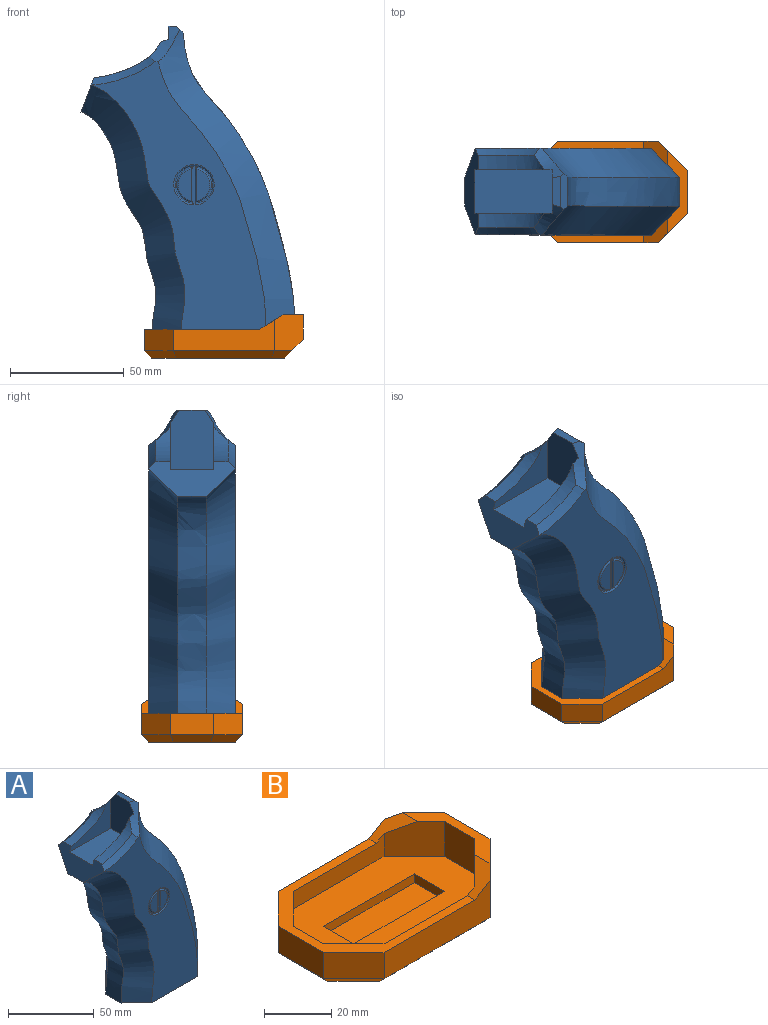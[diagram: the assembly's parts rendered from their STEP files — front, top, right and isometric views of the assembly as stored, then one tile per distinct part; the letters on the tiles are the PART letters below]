
ASSEMBLY  parts=2 mates=1
PART A: 44 faces, bbox 96.5x41.4x146.9 mm
  f0: plane 38.11x15.14mm, normal (-0.93,0,0.36), area 372.2mm2, adj f2,f3,f4,f9,f10,f13,f14,f15
  f1: plane 13.53x3.63mm, normal (0,0,1), area 45mm2, adj f16,f19,f20,f21
  f2: extruded ~29.2x15.61mm, area 194.8mm2, adj f0,f14,f18,f20
  f3: extruded ~29.2x15.61mm, area 194.9mm2, adj f0,f15,f17,f19
  f4: extruded ~101.84x33.05mm, area 1417.9mm2, adj f0,f5,f9,f10
  f5: plane 60.95x38.1mm, normal (0,0,-1), area 1573.9mm2, adj f4,f7,f8,f9,f10,f11,f12,f22
  f6: extruded ~133.98x49.47mm, area 1855.8mm2, adj f11,f12,f21,f43
  f7: plane 126.11x79.17mm, normal (0,-1,0), area 3830.8mm2, adj f5,f10,f12,f17,f19,f34
  f8: plane 126.11x79.17mm, normal (0,1,0), area 3832.2mm2, adj f5,f9,f11,f18,f20,f40
  f9: bspline ~118.13x45.8mm, area 2100.8mm2, adj f0,f4,f5,f8,f18
  f10: bspline ~118.13x45.8mm, area 2136.8mm2, adj f0,f4,f5,f7,f17
  f11: bspline ~138.88x62.18mm, area 2560.7mm2, adj f5,f6,f8,f20,f21,f43
  f12: bspline ~138.88x62.18mm, area 2560.7mm2, adj f5,f6,f7,f19,f21,f43
  f13: plane 33.95x19.05mm, normal (0,0,1), area 646.8mm2, adj f0,f14,f15,f16
  f14: plane 34.17x20.64mm, normal (0,-1,0), area 311.9mm2, adj f0,f2,f13,f16,f20
  f15: plane 34.17x20.64mm, normal (0,1,0), area 311.9mm2, adj f0,f3,f13,f16,f19
  f16: plane 26.8x19.58mm, normal (-1,0,0), area 478.3mm2, adj f1,f13,f14,f15,f19,f20
  f17: bspline ~30.63x14.14mm, area 128.4mm2, adj f0,f3,f7,f10,f19
  f18: bspline ~30.63x14.14mm, area 128.3mm2, adj f0,f2,f8,f9,f20
  f19: bspline ~17.85x15.06mm, area 103mm2, adj f1,f3,f7,f12,f15,f16,f17,f21
  f20: bspline ~17.86x15.07mm, area 103mm2, adj f1,f2,f8,f11,f14,f16,f18,f21
  f21: plane 16.15x3.24mm, normal (0.7,0,0.71), area 65.1mm2, adj f1,f6,f11,f12,f19,f20
  f22: plane 38.09x3.18mm, normal (0,-1,0), area 120.9mm2, adj f5,f23,f25,f26
  f23: plane 12.7x3.18mm, normal (-1,0,0), area 40.3mm2, adj f5,f22,f24,f26
  f24: plane 38.09x3.18mm, normal (0,1,0), area 120.9mm2, adj f5,f23,f25,f26
  f25: plane 12.7x3.18mm, normal (1,0,0), area 40.3mm2, adj f5,f22,f24,f26
  f26: plane 38.09x12.7mm, normal (0,0,-1), area 483.8mm2, adj f22,f23,f24,f25
  f27: plane 16.51x16.51mm, normal (0,-1,0), area 47.1mm2, adj f30,f31,f32,f33,f34
  f28: plane 13.78x5.84mm, normal (0,-1,0), area 60.7mm2, adj f32,f33
  f29: plane 13.78x5.84mm, normal (0,-1,0), area 60.7mm2, adj f30,f31
  f30: torus R=6.99mm, axis (0,-1,0), area 21.5mm2, adj f27,f29,f31
  f31: cylinder r=0.64mm len=15.21mm, axis (0,0,-1), area 14.5mm2, adj f27,f29,f30
  f32: cylinder r=0.64mm len=15.21mm, axis (0,0,1), area 14.5mm2, adj f27,f28,f33
  f33: torus R=6.99mm, axis (0,-1,0), area 21.5mm2, adj f27,f28,f32
  f34: torus R=8.89mm, axis (0,-1,0), area 53.2mm2, adj f7,f27
  f35: plane 16.51x16.51mm, normal (0,1,0), area 47.1mm2, adj f38,f39,f40,f41,f42
  f36: plane 13.78x5.84mm, normal (0,1,0), area 60.7mm2, adj f41,f42
  f37: plane 13.78x5.84mm, normal (0,1,0), area 60.7mm2, adj f38,f39
  f38: torus R=6.99mm, axis (0,-1,0), area 21.5mm2, adj f35,f37,f39
  f39: cylinder r=0.64mm len=15.21mm, axis (0,0,1), area 14.5mm2, adj f35,f37,f38
  f40: torus R=8.89mm, axis (0,-1,0), area 53.2mm2, adj f8,f35
  f41: cylinder r=0.64mm len=15.21mm, axis (0,0,-1), area 14.5mm2, adj f35,f36,f42
  f42: torus R=6.99mm, axis (0,-1,0), area 21.5mm2, adj f35,f36,f41
  f43: plane 17.83x2.59mm, normal (0.71,0,-0.7), area 55mm2, adj f5,f6,f11,f12
PART B: 35 faces, bbox 69.9x44.5x19.1 mm
  f0: plane 63.5x38.1mm, normal (0,0,1), area 1612.9mm2, adj f1,f2,f3,f4,f6,f7,f8,f9
  f1: plane 38.1x3.18mm, normal (0,-1,0), area 121mm2, adj f0,f2,f4,f5
  f2: plane 12.7x3.18mm, normal (1,0,0), area 40.3mm2, adj f0,f1,f3,f5
  f3: plane 38.1x3.18mm, normal (0,1,0), area 121mm2, adj f0,f2,f4,f5
  f4: plane 12.7x3.18mm, normal (-1,0,0), area 40.3mm2, adj f0,f1,f3,f5
  f5: plane 38.1x12.7mm, normal (0,0,1), area 483.9mm2, adj f1,f2,f3,f4
  f6: plane 12.7x12.7mm, normal (-1,0,0), area 161.3mm2, adj f0,f16,f19,f20
  f7: plane 38.1x8.33mm, normal (0,-1,0), area 245.1mm2, adj f0,f14,f17,f20,f22
  f8: plane 12.7x6.35mm, normal (1,0,0), area 80.6mm2, adj f0,f14,f21,f22
  f9: plane 38.1x8.33mm, normal (0,1,0), area 245.1mm2, adj f0,f14,f18,f19,f21
  f10: plane 44.45x13.49mm, normal (0,-1,0), area 436mm2, adj f14,f18,f25,f26,f28
  f11: plane 19.05x10.8mm, normal (1,0,0), area 205.6mm2, adj f16,f24,f25,f34
  f12: plane 44.45x13.49mm, normal (0,1,0), area 436mm2, adj f14,f17,f23,f24,f32
  f13: plane 19.05x9.53mm, normal (-1,0,0), area 181.5mm2, adj f14,f23,f26,f31
  f14: plane 50.8x44.45mm, normal (0,0,1), area 443.5mm2, adj f7,f8,f9,f10,f12,f13,f17,f18
  f15: plane 58.42x38.1mm, normal (0,0,-1), area 2075.1mm2, adj f27,f28,f29,f30,f31,f32,f33,f34
  f16: plane 36.83x8.89mm, normal (0,0,1), area 143.1mm2, adj f6,f11,f17,f18,f19,f20,f24,f25
  f17: plane 10.16x10.16mm, normal (-0.53,0,0.85), area 58.2mm2, adj f7,f12,f14,f16,f20,f24
  f18: plane 10.16x10.16mm, normal (-0.53,0,0.85), area 58.2mm2, adj f9,f10,f14,f16,f19,f25
  f19: plane 12.7x12.7mm, normal (-0.71,0.71,0), area 206.5mm2, adj f0,f6,f9,f16,f18
  f20: plane 12.7x12.7mm, normal (-0.71,-0.71,0), area 206.5mm2, adj f0,f6,f7,f16,f17
  f21: plane 12.7x12.7mm, normal (0.71,0.71,0), area 114mm2, adj f0,f8,f9,f14
  f22: plane 12.7x12.7mm, normal (0.71,-0.71,0), area 114mm2, adj f0,f7,f8,f14
  f23: plane 12.7x12.7mm, normal (-0.71,0.71,0), area 171.1mm2, adj f12,f13,f14,f33
  f24: plane 15.88x12.7mm, normal (0.71,0.71,0), area 260.5mm2, adj f11,f12,f16,f17,f30,f34
  f25: plane 15.88x12.7mm, normal (0.71,-0.71,0), area 260.5mm2, adj f10,f11,f16,f18,f27,f34
  f26: plane 12.7x12.7mm, normal (-0.71,-0.71,0), area 171.1mm2, adj f10,f13,f14,f29
  f27: plane 8.94x8.94mm, normal (0.5,-0.5,-0.71), area 42.5mm2, adj f15,f25,f28,f34
  f28: plane 44.45x3.18mm, normal (0,-0.71,-0.71), area 193.7mm2, adj f10,f15,f27,f29
  f29: plane 14.02x14.02mm, normal (-0.5,-0.5,-0.71), area 74.7mm2, adj f15,f26,f28,f31
  f30: plane 8.94x8.94mm, normal (0.5,0.5,-0.71), area 42.5mm2, adj f15,f24,f32,f34
  f31: plane 19.05x3.18mm, normal (-0.71,0,-0.71), area 79.6mm2, adj f13,f15,f29,f33
  f32: plane 44.45x3.18mm, normal (0,0.71,-0.71), area 193.7mm2, adj f12,f15,f30,f33
  f33: plane 14.02x14.02mm, normal (-0.5,0.5,-0.71), area 74.7mm2, adj f15,f23,f31,f32
  f34: plane 29.21x8.26mm, normal (0.71,0,-0.71), area 298.6mm2, adj f11,f15,f24,f25,f27,f30
PLACE A t=(-40.6,4.01,20.74)mm
PLACE B t=(-23.43,8.41,-33.02)mm
MATE fastened B.f5 <-> A.f26  axis (0,0,1) through (-18.28,4.01,-36.19)mm
